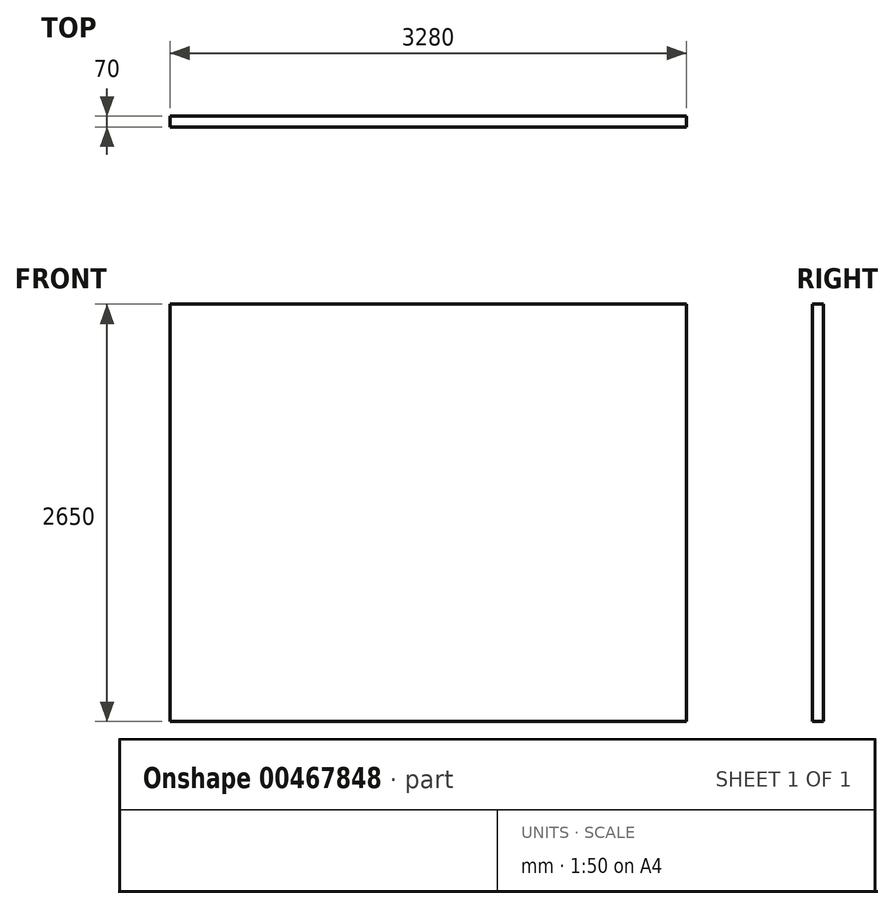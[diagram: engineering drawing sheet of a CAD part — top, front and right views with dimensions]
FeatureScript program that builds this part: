
annotation { "Feature Type Name" : "Feature", "Feature Type Description" : "" }
export const myFeature = defineFeature(function(context is Context, id is Id, definition is map)
    precondition{}
    {
        {
            var Q0;
            Q0=qCreatedBy(makeId("Front.planeOp"),FACE);
            var sketch = newSketch(context, id + "F0", { "sketchPlane" : qUnion([Q0])});
            skLineSegment(sketch, "E0.bottom", {"start": v(1640, -1325) * mm, "end": v(-1640, -1325) * mm});
            skLineSegment(sketch, "E0.top", {"start": v(1640, 1325) * mm, "end": v(-1640, 1325) * mm});
            skLineSegment(sketch, "E0.left", {"start": v(1640, -1325) * mm, "end": v(1640, 1325) * mm});
            skLineSegment(sketch, "E0.right", {"start": v(-1640, -1325) * mm, "end": v(-1640, 1325) * mm});
            skPoint(sketch, "E0.middle", {"position": v(0, 0) * mm});
            skSolve(sketch);
        }
        {
            var Q0;
            Q0=makeQuery(id+"F0.imprint","IMPRINT",FACE,{"disambiguationData":[TD([[makeQuery(id+"F0.imprint","IMPRINT",EDGE,{"derivedFrom":sQuery(id+"F0.wireOp",EDGE,"E0.bottom")}),-1.0]])]});
            extrude(context, id + "F1", {"entities" : qUnion([Q0]), "depth" : 70 * mm});
        }
    });
